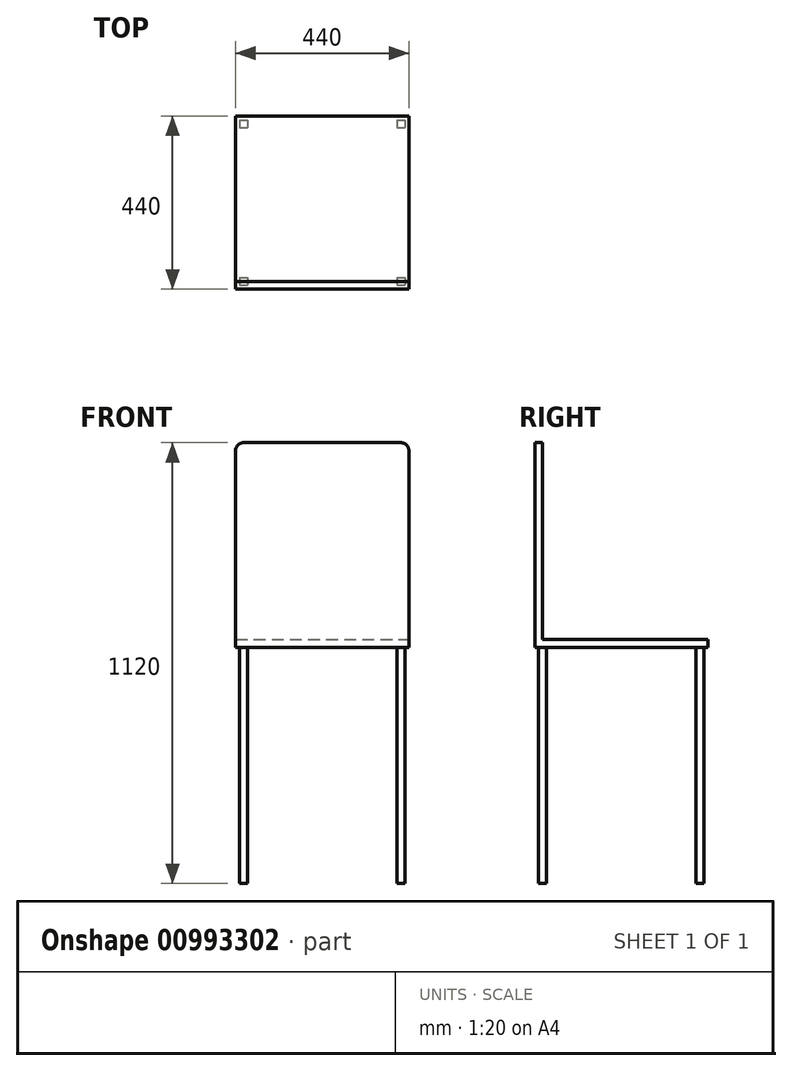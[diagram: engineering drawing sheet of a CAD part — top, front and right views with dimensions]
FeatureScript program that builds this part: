
annotation { "Feature Type Name" : "Feature", "Feature Type Description" : "" }
export const myFeature = defineFeature(function(context is Context, id is Id, definition is map)
    precondition{}
    {
        {
            var Q0;
            Q0=qCreatedBy(makeId("Top.planeOp"),FACE);
            var sketch = newSketch(context, id + "F0", { "sketchPlane" : qUnion([Q0])});
            skLineSegment(sketch, "E0.bottom", {"start": v(0, 20) * mm, "end": v(20, 20) * mm});
            skLineSegment(sketch, "E0.top", {"start": v(0, 0) * mm, "end": v(20, 0) * mm});
            skLineSegment(sketch, "E0.left", {"start": v(0, 20) * mm, "end": v(0, 0) * mm});
            skLineSegment(sketch, "E0.right", {"start": v(20, 20) * mm, "end": v(20, 0) * mm});
            skLineSegment(sketch, "E1.0.1.0", {"start": v(0, 420) * mm, "end": v(20, 420) * mm});
            skLineSegment(sketch, "E1.0.1.1", {"start": v(20, 420) * mm, "end": v(20, 400) * mm});
            skLineSegment(sketch, "E1.0.1.2", {"start": v(0, 400) * mm, "end": v(20, 400) * mm});
            skLineSegment(sketch, "E1.0.1.3", {"start": v(0, 420) * mm, "end": v(0, 400) * mm});
            skLineSegment(sketch, "E1.1.0.0", {"start": v(400, 20) * mm, "end": v(420, 20) * mm});
            skLineSegment(sketch, "E1.1.0.1", {"start": v(420, 20) * mm, "end": v(420, 0) * mm});
            skLineSegment(sketch, "E1.1.0.2", {"start": v(400, 0) * mm, "end": v(420, 0) * mm});
            skLineSegment(sketch, "E1.1.0.3", {"start": v(400, 20) * mm, "end": v(400, 0) * mm});
            skLineSegment(sketch, "E1.1.1.0", {"start": v(400, 420) * mm, "end": v(420, 420) * mm});
            skLineSegment(sketch, "E1.1.1.1", {"start": v(420, 420) * mm, "end": v(420, 400) * mm});
            skLineSegment(sketch, "E1.1.1.2", {"start": v(400, 400) * mm, "end": v(420, 400) * mm});
            skLineSegment(sketch, "E1.1.1.3", {"start": v(400, 420) * mm, "end": v(400, 400) * mm});
            skLineSegment(sketch, "E1.direction1", {"start": v(0, 20) * mm, "end": v(400, 20) * mm, "construction": true});
            skLineSegment(sketch, "E1.direction2", {"start": v(0, 20) * mm, "end": v(0, 420) * mm, "construction": true});
            skSolve(sketch);
        }
        {
            var Q0;
            Q0 = qSketchRegion(id + "F0", true);
            extrude(context, id + "F1", {"entities" : qUnion([Q0]), "depth" : 600 * mm, "offsetDistance" : 25 * mm});
        }
        {
            var Q0;
            Q0=makeQuery(id+"F1.opExtrude","CAP_FACE",FACE,{"disambiguationData":[OSD([sQuery(id+"F0.wireOp",EDGE,"E0.bottom"),sQuery(id+"F0.wireOp",EDGE,"E0.top"),sQuery(id+"F0.wireOp",EDGE,"E0.left"),sQuery(id+"F0.wireOp",EDGE,"E0.right")])],"isStart":false});
            var sketch = newSketch(context, id + "F2", { "sketchPlane" : qUnion([Q0])});
            skLineSegment(sketch, "E2.bottom", {"start": v(-10, 430) * mm, "end": v(430, 430) * mm});
            skLineSegment(sketch, "E2.top", {"start": v(-10, -10) * mm, "end": v(430, -10) * mm});
            skLineSegment(sketch, "E2.left", {"start": v(-10, 430) * mm, "end": v(-10, -10) * mm});
            skLineSegment(sketch, "E2.right", {"start": v(430, 430) * mm, "end": v(430, -10) * mm});
            skSolve(sketch);
        }
        {
            var Q0;
            Q0 = qSketchRegion(id + "F2", true);
            extrude(context, id + "F3", {"entities" : qUnion([Q0]), "operationType" : NewBodyOperationType.ADD, "depth" : 20 * mm, "offsetDistance" : 25 * mm});
        }
        {
            var Q0;
            Q0=makeQuery(id+"F3.opExtrude","CAP_FACE",FACE,{"disambiguationData":[OSD([sQuery(id+"F2.wireOp",EDGE,"E2.bottom"),sQuery(id+"F2.wireOp",EDGE,"E2.top"),sQuery(id+"F2.wireOp",EDGE,"E2.left"),sQuery(id+"F2.wireOp",EDGE,"E2.right")])],"isStart":false});
            var sketch = newSketch(context, id + "F4", { "sketchPlane" : qUnion([Q0])});
            skLineSegment(sketch, "E3.bottom", {"start": v(-10, -10) * mm, "end": v(430, -10) * mm});
            skLineSegment(sketch, "E3.top", {"start": v(-10, 10) * mm, "end": v(430, 10) * mm});
            skLineSegment(sketch, "E3.left", {"start": v(-10, -10) * mm, "end": v(-10, 10) * mm});
            skLineSegment(sketch, "E3.right", {"start": v(430, -10) * mm, "end": v(430, 10) * mm});
            skSolve(sketch);
        }
        {
            var Q0;
            Q0 = qSketchRegion(id + "F4", true);
            extrude(context, id + "F5", {"entities" : qUnion([Q0]), "operationType" : NewBodyOperationType.ADD, "depth" : 500 * mm, "offsetDistance" : 25 * mm});
        }
        {
            var Q0;
            Q0=makeQuery(id+"F5.opExtrude","CAP_EDGE",EDGE,{"disambiguationData":[OSD([sQuery(id+"F4.wireOp",EDGE,"E3.right")])],"isStart":false});
            var Q1;
            Q1=makeQuery(id+"F5.opExtrude","CAP_EDGE",EDGE,{"disambiguationData":[OSD([sQuery(id+"F4.wireOp",EDGE,"E3.left")])],"isStart":false});
            fillet(context, id + "F6", {"entities" : qUnion([Q0, Q1]), "radius" : 20 * mm, "tangentPropagation" : true, "allowEdgeOverflow" : false});
        }
    });
